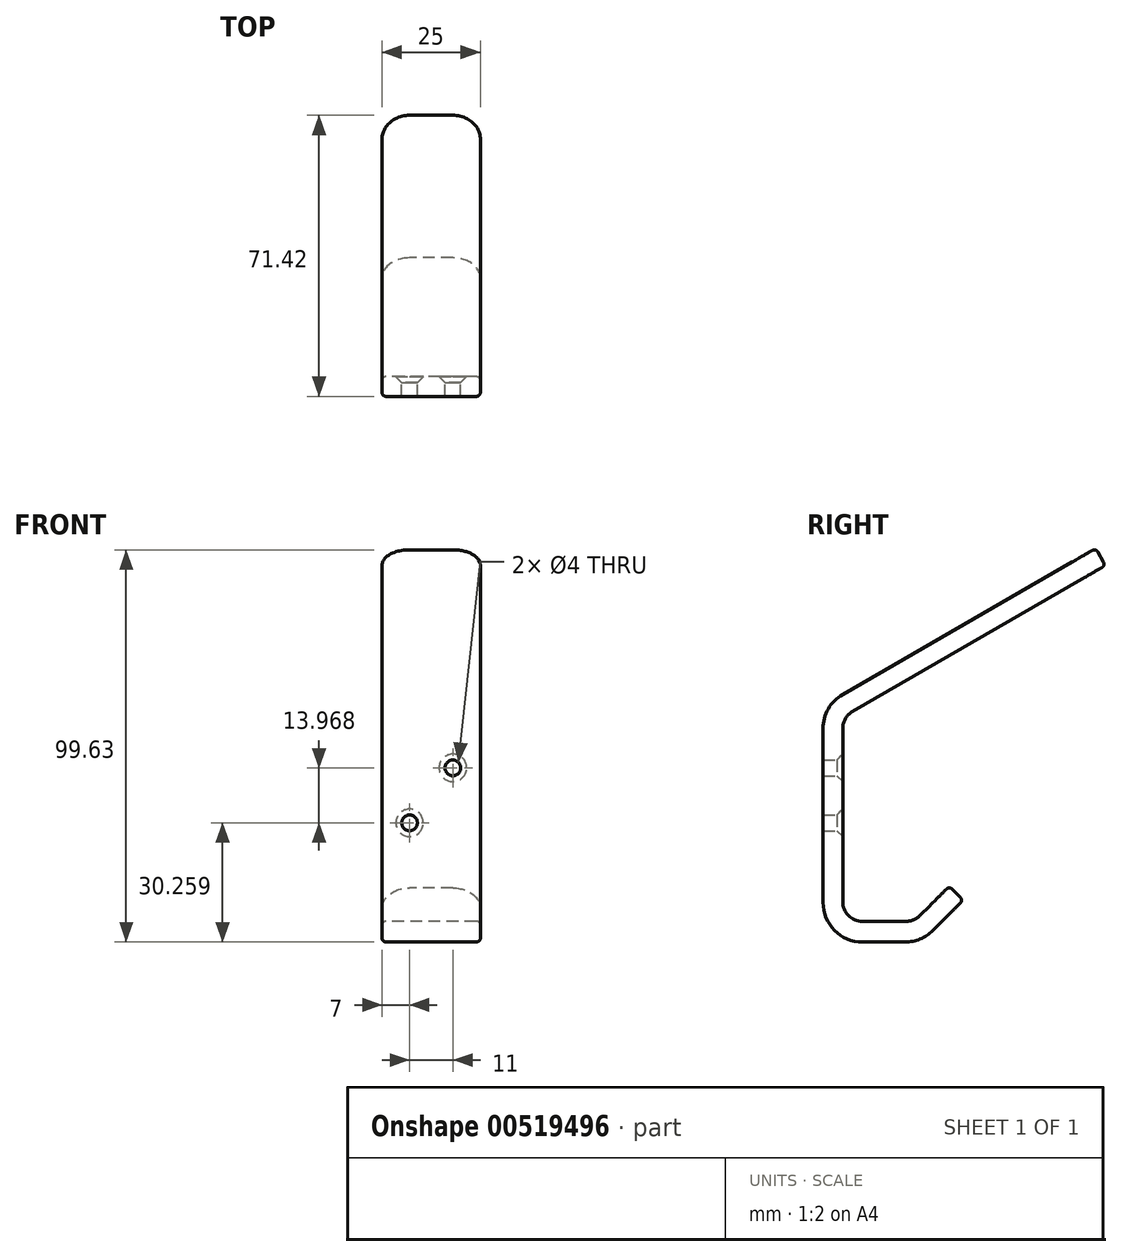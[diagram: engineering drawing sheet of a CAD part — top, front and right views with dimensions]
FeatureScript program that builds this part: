
annotation { "Feature Type Name" : "Feature", "Feature Type Description" : "" }
export const myFeature = defineFeature(function(context is Context, id is Id, definition is map)
    precondition{}
    {
        {
            var Q0;
            Q0=qCreatedBy(makeId("Right.planeOp"),FACE);
            var sketch = newSketch(context, id + "F0", { "sketchPlane" : qUnion([Q0])});
            skLineSegment(sketch, "E0", {"start": v(-25, 0) * mm, "end": v(-25, 60) * mm});
            skLineSegment(sketch, "E1", {"start": v(-20, 5.26) * mm, "end": v(-20, 57.11) * mm});
            skLineSegment(sketch, "E2", {"start": v(44.28, 100) * mm, "end": v(46.78, 95.67) * mm});
            skLineSegment(sketch, "E3", {"start": v(46.78, 95.67) * mm, "end": v(-20, 57.11) * mm});
            skLineSegment(sketch, "E4", {"start": v(44.28, 100) * mm, "end": v(-25, 60) * mm});
            skLineSegment(sketch, "E5", {"start": v(-25, 0) * mm, "end": v(0, 0) * mm});
            skLineSegment(sketch, "E6", {"start": v(0, 0) * mm, "end": v(10.6, 10.6) * mm});
            skLineSegment(sketch, "E7", {"start": v(10.6, 10.6) * mm, "end": v(7.07, 14.14) * mm});
            skLineSegment(sketch, "E8", {"start": v(7.07, 14.14) * mm, "end": v(-1.81, 5.26) * mm});
            skLineSegment(sketch, "E9", {"start": v(-20, 5.26) * mm, "end": v(-1.81, 5.26) * mm});
            skSolve(sketch);
        }
        {
            var Q0;
            Q0=makeQuery(id+"F0.imprint","IMPRINT",FACE,{"disambiguationData":[TD([[makeQuery(id+"F0.imprint","IMPRINT",EDGE,{"derivedFrom":sQuery(id+"F0.wireOp",EDGE,"E0")}),-1.0]])]});
            extrude(context, id + "F1", {"entities" : qUnion([Q0]), "depth" : 25 * mm, "offsetDistance" : 25 * mm});
        }
        {
            var Q0;
            Q0=makeQuery(id+"F1.opExtrude","CAP_EDGE",EDGE,{"disambiguationData":[OSD([sQuery(id+"F0.wireOp",EDGE,"E7")])],"isStart":false});
            var Q1;
            Q1=makeQuery(id+"F1.opExtrude","CAP_EDGE",EDGE,{"disambiguationData":[OSD([sQuery(id+"F0.wireOp",EDGE,"E7")])],"isStart":true});
            var Q2;
            Q2=makeQuery(id+"F1.opExtrude","CAP_EDGE",EDGE,{"disambiguationData":[OSD([sQuery(id+"F0.wireOp",EDGE,"E2")])],"isStart":false});
            var Q3;
            Q3=makeQuery(id+"F1.opExtrude","CAP_EDGE",EDGE,{"disambiguationData":[OSD([sQuery(id+"F0.wireOp",EDGE,"E2")])],"isStart":true});
            fillet(context, id + "F2", {"entities" : qUnion([Q0, Q1, Q2, Q3]), "radius" : 7 * mm, "tangentPropagation" : true, "allowEdgeOverflow" : false});
        }
        {
            var Q0;
            Q0=makeQuery(id+"F1.opExtrude","SWEPT_EDGE",EDGE,{"disambiguationData":[OSD([sQuery(id+"F0.wireOp",EDGE,"E1"),sQuery(id+"F0.wireOp",EDGE,"E3")])]});
            fillet(context, id + "F3", {"entities" : qUnion([Q0]), "radius" : 5 * mm, "tangentPropagation" : true, "allowEdgeOverflow" : false});
        }
        {
            var Q0;
            Q0=makeQuery(id+"F1.opExtrude","SWEPT_EDGE",EDGE,{"disambiguationData":[OSD([sQuery(id+"F0.wireOp",EDGE,"E0"),sQuery(id+"F0.wireOp",EDGE,"E4")])]});
            fillet(context, id + "F4", {"entities" : qUnion([Q0]), "radius" : 10 * mm, "tangentPropagation" : true, "allowEdgeOverflow" : false});
        }
        {
            var Q0;
            Q0=makeQuery(id+"F1.opExtrude","SWEPT_EDGE",EDGE,{"disambiguationData":[OSD([sQuery(id+"F0.wireOp",EDGE,"E8"),sQuery(id+"F0.wireOp",EDGE,"E9")])]});
            fillet(context, id + "F5", {"entities" : qUnion([Q0]), "radius" : 5 * mm, "tangentPropagation" : true, "allowEdgeOverflow" : false});
        }
        {
            var Q0;
            Q0=makeQuery(id+"F1.opExtrude","SWEPT_EDGE",EDGE,{"disambiguationData":[OSD([sQuery(id+"F0.wireOp",EDGE,"E0"),sQuery(id+"F0.wireOp",EDGE,"E5")])]});
            fillet(context, id + "F6", {"entities" : qUnion([Q0]), "radius" : 10 * mm, "tangentPropagation" : true, "allowEdgeOverflow" : false});
        }
        {
            var Q0;
            Q0=makeQuery(id+"F1.opExtrude","SWEPT_EDGE",EDGE,{"disambiguationData":[OSD([sQuery(id+"F0.wireOp",EDGE,"E5"),sQuery(id+"F0.wireOp",EDGE,"E6")])]});
            fillet(context, id + "F7", {"entities" : qUnion([Q0]), "radius" : 10 * mm, "tangentPropagation" : true, "allowEdgeOverflow" : false});
        }
        {
            var Q0;
            Q0=makeQuery(id+"F1.opExtrude","CAP_EDGE",EDGE,{"disambiguationData":[OSD([sQuery(id+"F0.wireOp",EDGE,"E0")])],"isStart":true});
            fillet(context, id + "F8", {"entities" : qUnion([Q0]), "radius" : 1 * mm, "tangentPropagation" : true, "allowEdgeOverflow" : false});
        }
        {
            var Q0;
            Q0=makeQuery(id+"F1.opExtrude","SWEPT_EDGE",EDGE,{"disambiguationData":[OSD([sQuery(id+"F0.wireOp",EDGE,"E1"),sQuery(id+"F0.wireOp",EDGE,"E9")])]});
            fillet(context, id + "F9", {"entities" : qUnion([Q0]), "radius" : 5 * mm, "tangentPropagation" : true, "allowEdgeOverflow" : false});
        }
        {
            var Q0;
            Q0=makeQuery(id+"F1.opExtrude","CAP_EDGE",EDGE,{"disambiguationData":[OSD([sQuery(id+"F0.wireOp",EDGE,"E1")])],"isStart":false});
            fillet(context, id + "F10", {"entities" : qUnion([Q0]), "radius" : 1 * mm, "tangentPropagation" : true, "allowEdgeOverflow" : false});
        }
        {
            var Q0;
            Q0=makeQuery(id+"F1.opExtrude","SWEPT_FACE",FACE,{"disambiguationData":[OSD([sQuery(id+"F0.wireOp",EDGE,"E1")])]});
            var sketch = newSketch(context, id + "F11", { "sketchPlane" : qUnion([Q0])});
            skPoint(sketch, "E10", {"position": v(-18, 44.23) * mm});
            skPoint(sketch, "E11", {"position": v(-7, 30.26) * mm});
            skSolve(sketch);
        }
        {
            var Q0;
            Q0=sQuery(id+"F11.wireOp",VERTEX,"E10");
            var Q1;
            Q1=sQuery(id+"F11.wireOp",VERTEX,"E11");
            var Q2;
            Q2=makeQuery(id+"F1.opExtrude","SWEPT_BODY",BODY,{"disambiguationData":[OSD([sQuery(id+"F0.wireOp",EDGE,"E0"),sQuery(id+"F0.wireOp",EDGE,"E1"),sQuery(id+"F0.wireOp",EDGE,"E2"),sQuery(id+"F0.wireOp",EDGE,"E3"),sQuery(id+"F0.wireOp",EDGE,"E4"),sQuery(id+"F0.wireOp",EDGE,"E5"),sQuery(id+"F0.wireOp",EDGE,"E6"),sQuery(id+"F0.wireOp",EDGE,"E7"),sQuery(id+"F0.wireOp",EDGE,"E8"),sQuery(id+"F0.wireOp",EDGE,"E9")])]});
            hole(context, id + "F12", {"style" : HoleStyle.C_SINK, "endStyle" : HoleEndStyle.THROUGH, "holeDiameter" : 4 * mm, "cSinkDiameter" : 7 * mm, "cSinkAngle" : 90 * degree, "isTappedThrough" : true, "tappedDepth" : 12 * mm, "tapClearance" : 3, "locations" : qUnion([Q0, Q1]), "scope" : qUnion([Q2])});
        }
    });
